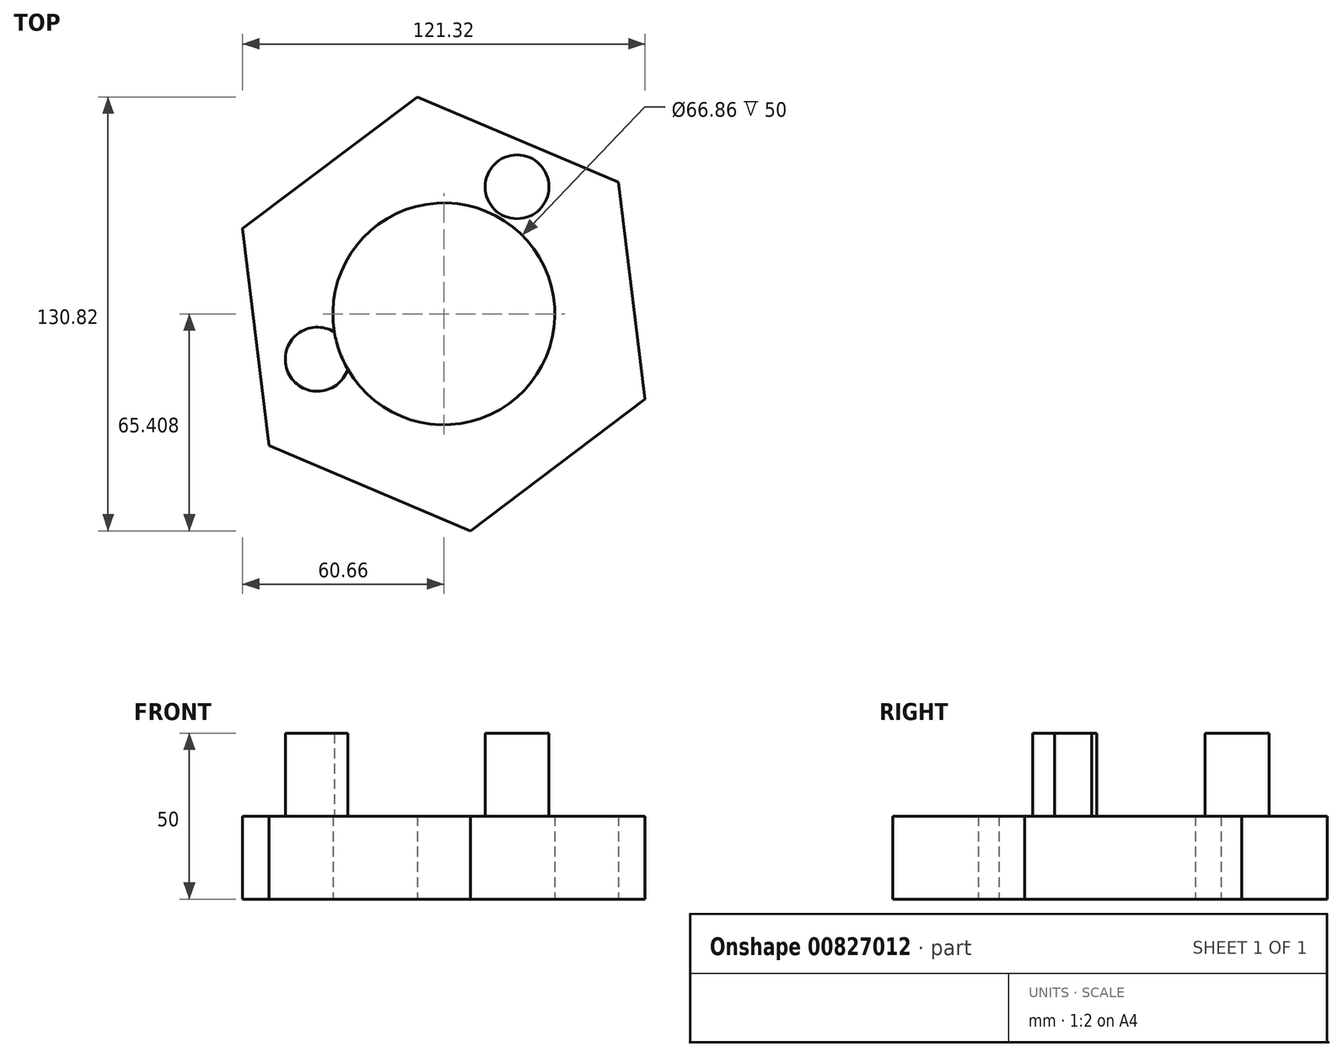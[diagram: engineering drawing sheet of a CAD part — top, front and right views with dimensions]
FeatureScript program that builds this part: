
annotation { "Feature Type Name" : "Feature", "Feature Type Description" : "" }
export const myFeature = defineFeature(function(context is Context, id is Id, definition is map)
    precondition{}
    {
        {
            var Q0;
            Q0=qCreatedBy(makeId("Top.planeOp"),FACE);
            var sketch = newSketch(context, id + "F0", { "sketchPlane" : qUnion([Q0])});
            skCircle(sketch, "E0", {"center": v(0, -4.1) * mm, "radius": 33.43 * mm});
            skCircle(sketch, "E1.cCircle", {"center": v(0, -4.1) * mm, "radius": 57.07 * mm, "construction": true});
            skLineSegment(sketch, "E1.0", {"start": v(-60.66, 21.66) * mm, "end": v(-8.02, 61.3) * mm});
            skLineSegment(sketch, "E1.1", {"start": v(-8.02, 61.3) * mm, "end": v(52.64, 35.55) * mm});
            skLineSegment(sketch, "E1.2", {"start": v(52.64, 35.55) * mm, "end": v(60.66, -29.86) * mm});
            skLineSegment(sketch, "E1.3", {"start": v(60.66, -29.86) * mm, "end": v(8.02, -69.51) * mm});
            skLineSegment(sketch, "E1.4", {"start": v(8.02, -69.51) * mm, "end": v(-52.64, -43.75) * mm});
            skLineSegment(sketch, "E1.5", {"start": v(-52.64, -43.75) * mm, "end": v(-60.66, 21.66) * mm});
            skPoint(sketch, "E1.0.midPoint", {"position": v(-34.34, 41.48) * mm});
            skSolve(sketch);
        }
        {
            var Q0;
            Q0=makeQuery(id+"F0.imprint","IMPRINT",FACE,{"disambiguationData":[TD([[makeQuery(id+"F0.imprint","IMPRINT",EDGE,{"derivedFrom":sQuery(id+"F0.wireOp",EDGE,"E0")}),-1.0]])]});
            extrude(context, id + "F1", {"entities" : qUnion([Q0]), "depth" : 25 * mm, "offsetDistance" : 25 * mm});
        }
        {
            var Q0;
            Q0=makeQuery(id+"F1.opExtrude","CAP_FACE",FACE,{"disambiguationData":[OSD([sQuery(id+"F0.wireOp",EDGE,"E0"),sQuery(id+"F0.wireOp",EDGE,"E1.0"),sQuery(id+"F0.wireOp",EDGE,"E1.1"),sQuery(id+"F0.wireOp",EDGE,"E1.2"),sQuery(id+"F0.wireOp",EDGE,"E1.3"),sQuery(id+"F0.wireOp",EDGE,"E1.4"),sQuery(id+"F0.wireOp",EDGE,"E1.5")])],"isStart":false});
            var sketch = newSketch(context, id + "F2", { "sketchPlane" : qUnion([Q0])});
            skCircle(sketch, "E2", {"center": v(-38.12, -17.8) * mm, "radius": 9.66 * mm});
            skCircle(sketch, "E3", {"center": v(22.07, 34.18) * mm, "radius": 9.62 * mm});
            skSolve(sketch);
        }
        {
            var Q0;
            {var subQ0=sQuery(id+"F2.wireOp",EDGE,"E2");var subQ1=makeQuery(id+"F1.opExtrude","CAP_EDGE",EDGE,{"disambiguationData":[OSD([sQuery(id+"F0.wireOp",EDGE,"E0")])],"isStart":false});var subQ2=makeQuery(id+"F2.imprint","INTERSECT",VERTEX,{"disambiguationData":[OD(0.0)],"derivedFrom":[subQ1,subQ0]});Q0=makeQuery(id+"F2.imprint","IMPRINT",FACE,{"disambiguationData":[TD([[makeQuery(id+"F2.imprint","IMPRINT",EDGE,{"disambiguationData":[TD([[subQ2,1.0]])],"derivedFrom":subQ0}),1.0]])]});}
            var Q1;
            Q1=makeQuery(id+"F2.imprint","IMPRINT",FACE,{"disambiguationData":[TD([[makeQuery(id+"F2.imprint","IMPRINT",EDGE,{"derivedFrom":sQuery(id+"F2.wireOp",EDGE,"E3")}),1.0]])]});
            extrude(context, id + "F3", {"entities" : qUnion([Q0, Q1]), "operationType" : NewBodyOperationType.ADD, "depth" : 25 * mm, "offsetDistance" : 25 * mm});
        }
    });
